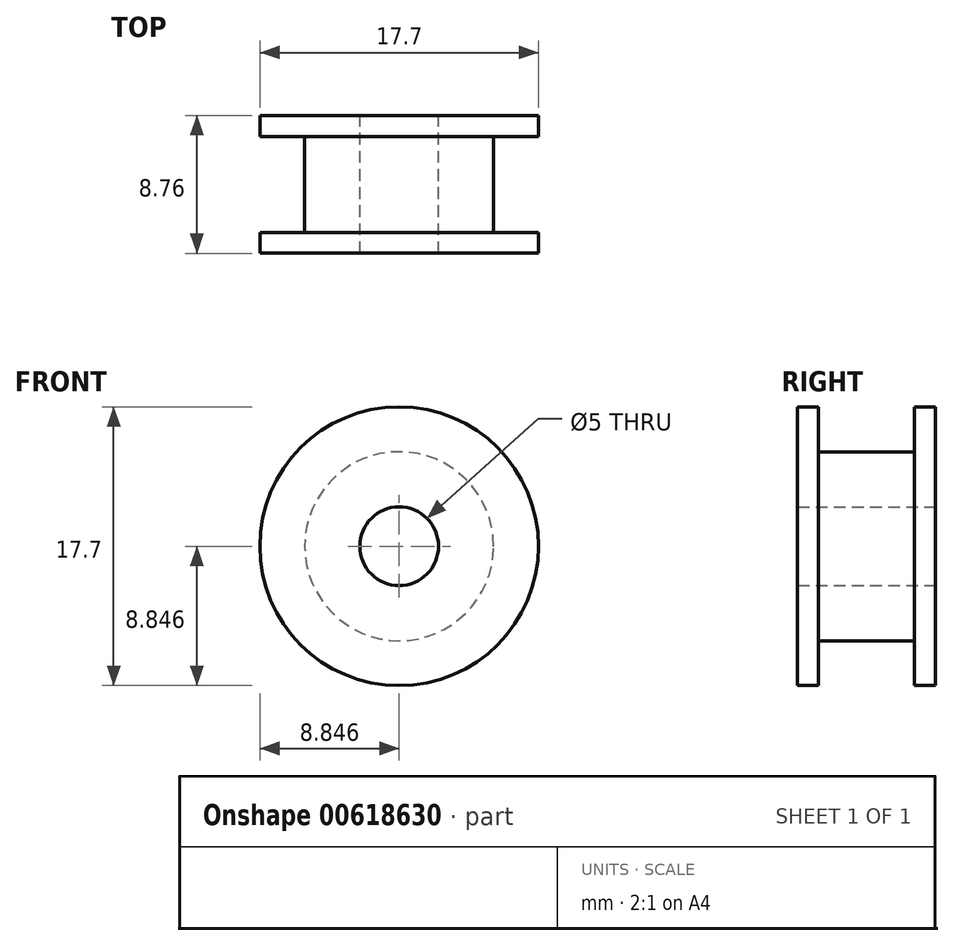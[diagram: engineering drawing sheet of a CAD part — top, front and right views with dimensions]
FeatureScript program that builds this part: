
annotation { "Feature Type Name" : "Feature", "Feature Type Description" : "" }
export const myFeature = defineFeature(function(context is Context, id is Id, definition is map)
    precondition{}
    {
        {
            var Q0;
            Q0=qCreatedBy(makeId("Front.planeOp"),FACE);
            var sketch = newSketch(context, id + "F0", { "sketchPlane" : qUnion([Q0])});
            skCircle(sketch, "E0", {"center": v(-54.15, 41.9) * mm, "radius": 8.85 * mm});
            skCircle(sketch, "E1", {"center": v(-54.15, 41.9) * mm, "radius": 2.5 * mm});
            skCircle(sketch, "E2", {"center": v(-54.15, 41.9) * mm, "radius": 6 * mm});
            skSolve(sketch);
        }
        {
            var Q0;
            Q0=makeQuery(id+"F0.imprint","IMPRINT",FACE,{"disambiguationData":[TD([[makeQuery(id+"F0.imprint","IMPRINT",EDGE,{"derivedFrom":sQuery(id+"F0.wireOp",EDGE,"E0")}),1.0]])]});
            var Q1;
            Q1=makeQuery(id+"F0.imprint","IMPRINT",FACE,{"disambiguationData":[TD([[makeQuery(id+"F0.imprint","IMPRINT",EDGE,{"derivedFrom":sQuery(id+"F0.wireOp",EDGE,"E1")}),-1.0]])]});
            extrude(context, id + "F1", {"entities" : qUnion([Q0, Q1]), "endBound" : BoundingType.SYMMETRIC, "depth" : 8.75 * mm, "offsetDistance" : 25 * mm});
        }
        {
            var Q0;
            Q0=makeQuery(id+"F0.imprint","IMPRINT",FACE,{"disambiguationData":[TD([[makeQuery(id+"F0.imprint","IMPRINT",EDGE,{"derivedFrom":sQuery(id+"F0.wireOp",EDGE,"E0")}),1.0]])]});
            extrude(context, id + "F2", {"entities" : qUnion([Q0]), "operationType" : NewBodyOperationType.REMOVE, "endBound" : BoundingType.SYMMETRIC, "depth" : 6.1 * mm, "offsetDistance" : 25 * mm});
        }
    });
